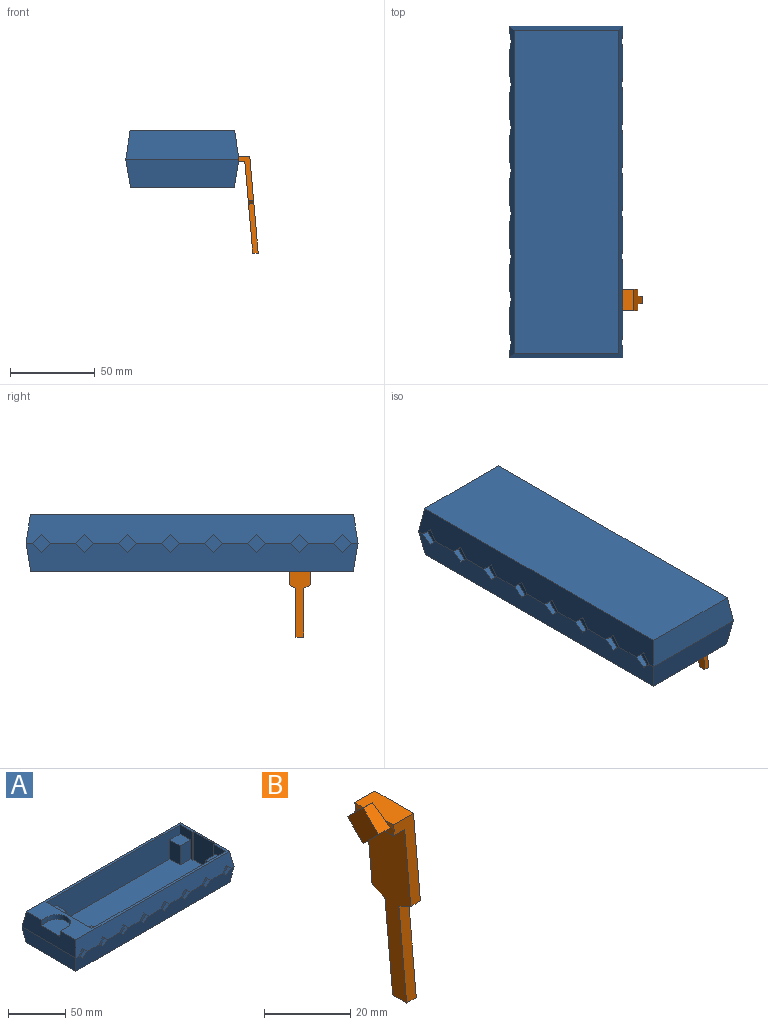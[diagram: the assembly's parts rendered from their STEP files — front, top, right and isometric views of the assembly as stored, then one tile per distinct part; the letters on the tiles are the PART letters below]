
ASSEMBLY  parts=2 mates=1
PART A: 115 faces, bbox 195.6x66.7x33.3 mm
  f0: plane 166.78x56.39mm, normal (0,0,1), area 8723mm2, adj f1,f2,f3,f12,f16,f17,f61,f62
  f1: plane 165.61x30.1mm, normal (0,1,0), area 4465.3mm2, adj f0,f3,f5,f62,f109,f111,f112,f114
  f2: plane 165.61x30.1mm, normal (0,-1,0), area 4465.3mm2, adj f0,f3,f5,f17,f103,f105,f106,f108
  f3: plane 56.39x30.1mm, normal (1,0,0), area 1177.9mm2, adj f0,f1,f2,f5,f103,f104,f112,f113
  f4: plane 190.5x61.6mm, normal (0,0,-1), area 11733.8mm2, adj f8,f9,f14,f59
  f5: plane 189.99x61.09mm, normal (0,0,1), area 1854.9mm2, adj f1,f2,f3,f6,f7,f10,f12,f13
  f6: plane 66.68x16.64mm, normal (-0.99,0,0.17), area 958.6mm2, adj f5,f8,f11,f13,f15,f58,f60
  f7: plane 66.68x16.64mm, normal (0.99,0,0.17), area 1077.7mm2, adj f5,f9,f13,f58
  f8: plane 66.68x16.64mm, normal (-0.99,0,-0.15), area 1079.4mm2, adj f4,f6,f14,f59
  f9: plane 66.68x16.64mm, normal (0.99,0,-0.15), area 1079.4mm2, adj f4,f7,f14,f59
  f10: cylinder r=11.56mm len=23.11mm, axis (0,0,1), area 184.4mm2, adj f5,f11,f15,f60
  f11: plane 23.11x19.9mm, normal (0,0,1), area 402.7mm2, adj f6,f10,f15,f60
  f12: plane 30.1x25.4mm, normal (-1,0,0), area 764.5mm2, adj f0,f5,f16,f61
  f13: plane 195.58x16.64mm, normal (0,0.99,0.17), area 3021.5mm2, adj f5,f6,f7,f14,f19,f21,f24,f26
  f14: plane 195.58x16.64mm, normal (0,0.99,-0.15), area 3018.6mm2, adj f4,f8,f9,f13,f20,f22,f25,f27
  f15: plane 8.35x5.08mm, normal (0,-1,0), area 40.2mm2, adj f5,f6,f10,f11
  f16: plane 30.1x1.17mm, normal (0,-1,0), area 35.4mm2, adj f0,f5,f12,f17
  f17: plane 30.1x15.49mm, normal (-1,0,0), area 206.7mm2, adj f0,f2,f5,f16,f106,f107
  f18: plane 10.67x10.67mm, normal (0,1,0), area 56.9mm2, adj f19,f20,f21,f22
  f19: plane 5.33x5.33mm, normal (0.71,0,-0.71), area 25.8mm2, adj f13,f18,f20,f21
  f20: plane 5.33x5.33mm, normal (0.71,0,0.71), area 26.1mm2, adj f14,f18,f19,f22
  f21: plane 5.33x5.33mm, normal (-0.71,0,-0.71), area 25.8mm2, adj f13,f18,f19,f22
  f22: plane 5.33x5.33mm, normal (-0.71,0,0.71), area 26.1mm2, adj f14,f18,f20,f21
  f23: plane 10.67x10.67mm, normal (0,1,0), area 56.9mm2, adj f24,f25,f26,f27
  f24: plane 5.33x5.33mm, normal (0.71,0,-0.71), area 25.8mm2, adj f13,f23,f25,f26
  f25: plane 5.33x5.33mm, normal (0.71,0,0.71), area 26.1mm2, adj f14,f23,f24,f27
  f26: plane 5.33x5.33mm, normal (-0.71,0,-0.71), area 25.8mm2, adj f13,f23,f24,f27
  f27: plane 5.33x5.33mm, normal (-0.71,0,0.71), area 26.1mm2, adj f14,f23,f25,f26
  f28: plane 10.67x10.67mm, normal (0,1,0), area 56.9mm2, adj f29,f30,f31,f32
  f29: plane 5.33x5.33mm, normal (0.71,0,-0.71), area 25.8mm2, adj f13,f28,f30,f31
  f30: plane 5.33x5.33mm, normal (0.71,0,0.71), area 26.1mm2, adj f14,f28,f29,f32
  f31: plane 5.33x5.33mm, normal (-0.71,0,-0.71), area 25.8mm2, adj f13,f28,f29,f32
  f32: plane 5.33x5.33mm, normal (-0.71,0,0.71), area 26.1mm2, adj f14,f28,f30,f31
  f33: plane 10.67x10.67mm, normal (0,1,0), area 56.9mm2, adj f34,f35,f36,f37
  f34: plane 5.33x5.33mm, normal (0.71,0,-0.71), area 25.8mm2, adj f13,f33,f35,f36
  f35: plane 5.33x5.33mm, normal (0.71,0,0.71), area 26.1mm2, adj f14,f33,f34,f37
  f36: plane 5.33x5.33mm, normal (-0.71,0,-0.71), area 25.8mm2, adj f13,f33,f34,f37
  f37: plane 5.33x5.33mm, normal (-0.71,0,0.71), area 26.1mm2, adj f14,f33,f35,f36
  f38: plane 10.67x10.67mm, normal (0,1,0), area 56.9mm2, adj f39,f40,f41,f42
  f39: plane 5.33x5.33mm, normal (0.71,0,-0.71), area 25.8mm2, adj f13,f38,f40,f41
  f40: plane 5.33x5.33mm, normal (0.71,0,0.71), area 26.1mm2, adj f14,f38,f39,f42
  f41: plane 5.33x5.33mm, normal (-0.71,0,-0.71), area 25.8mm2, adj f13,f38,f39,f42
  f42: plane 5.33x5.33mm, normal (-0.71,0,0.71), area 26.1mm2, adj f14,f38,f40,f41
  f43: plane 10.67x10.67mm, normal (0,1,0), area 56.9mm2, adj f44,f45,f46,f47
  f44: plane 5.33x5.33mm, normal (0.71,0,-0.71), area 25.8mm2, adj f13,f43,f45,f46
  f45: plane 5.33x5.33mm, normal (0.71,0,0.71), area 26.1mm2, adj f14,f43,f44,f47
  f46: plane 5.33x5.33mm, normal (-0.71,0,-0.71), area 25.8mm2, adj f13,f43,f44,f47
  f47: plane 5.33x5.33mm, normal (-0.71,0,0.71), area 26.1mm2, adj f14,f43,f45,f46
  f48: plane 10.67x10.67mm, normal (0,1,0), area 56.9mm2, adj f49,f50,f51,f52
  f49: plane 5.33x5.33mm, normal (0.71,0,-0.71), area 25.8mm2, adj f13,f48,f50,f51
  f50: plane 5.33x5.33mm, normal (0.71,0,0.71), area 26.1mm2, adj f14,f48,f49,f52
  f51: plane 5.33x5.33mm, normal (-0.71,0,-0.71), area 25.8mm2, adj f13,f48,f49,f52
  f52: plane 5.33x5.33mm, normal (-0.71,0,0.71), area 26.1mm2, adj f14,f48,f50,f51
  f53: plane 10.67x10.67mm, normal (0,1,0), area 56.9mm2, adj f54,f55,f56,f57
  f54: plane 5.33x5.33mm, normal (0.71,0,0.71), area 26.1mm2, adj f14,f53,f55,f56
  f55: plane 5.33x5.33mm, normal (-0.71,0,0.71), area 26.1mm2, adj f14,f53,f54,f57
  f56: plane 5.33x5.33mm, normal (0.71,0,-0.71), area 25.8mm2, adj f13,f53,f54,f57
  f57: plane 5.33x5.33mm, normal (-0.71,0,-0.71), area 25.8mm2, adj f13,f53,f55,f56
  f58: plane 195.58x16.64mm, normal (0,-0.99,0.17), area 3021.5mm2, adj f5,f6,f7,f59,f64,f66,f69,f71
  f59: plane 195.58x16.64mm, normal (0,-0.99,-0.15), area 3018.6mm2, adj f4,f8,f9,f58,f65,f67,f70,f72
  f60: plane 8.35x5.08mm, normal (0,1,0), area 40.2mm2, adj f5,f6,f10,f11
  f61: plane 30.1x1.17mm, normal (0,1,0), area 35.4mm2, adj f0,f5,f12,f62
  f62: plane 30.1x15.49mm, normal (-1,0,0), area 206.7mm2, adj f0,f1,f5,f61,f109,f110
  f63: plane 10.67x10.67mm, normal (0,-1,0), area 56.9mm2, adj f64,f65,f66,f67
  f64: plane 5.33x5.33mm, normal (0.71,0,-0.71), area 25.8mm2, adj f58,f63,f65,f66
  f65: plane 5.33x5.33mm, normal (0.71,0,0.71), area 26.1mm2, adj f59,f63,f64,f67
  f66: plane 5.33x5.33mm, normal (-0.71,0,-0.71), area 25.8mm2, adj f58,f63,f64,f67
  f67: plane 5.33x5.33mm, normal (-0.71,0,0.71), area 26.1mm2, adj f59,f63,f65,f66
  f68: plane 10.67x10.67mm, normal (0,-1,0), area 56.9mm2, adj f69,f70,f71,f72
  f69: plane 5.33x5.33mm, normal (0.71,0,-0.71), area 25.8mm2, adj f58,f68,f70,f71
  f70: plane 5.33x5.33mm, normal (0.71,0,0.71), area 26.1mm2, adj f59,f68,f69,f72
  f71: plane 5.33x5.33mm, normal (-0.71,0,-0.71), area 25.8mm2, adj f58,f68,f69,f72
  f72: plane 5.33x5.33mm, normal (-0.71,0,0.71), area 26.1mm2, adj f59,f68,f70,f71
  f73: plane 10.67x10.67mm, normal (0,-1,0), area 56.9mm2, adj f74,f75,f76,f77
  f74: plane 5.33x5.33mm, normal (0.71,0,-0.71), area 25.8mm2, adj f58,f73,f75,f76
  f75: plane 5.33x5.33mm, normal (0.71,0,0.71), area 26.1mm2, adj f59,f73,f74,f77
  f76: plane 5.33x5.33mm, normal (-0.71,0,-0.71), area 25.8mm2, adj f58,f73,f74,f77
  f77: plane 5.33x5.33mm, normal (-0.71,0,0.71), area 26.1mm2, adj f59,f73,f75,f76
  f78: plane 10.67x10.67mm, normal (0,-1,0), area 56.9mm2, adj f79,f80,f81,f82
  f79: plane 5.33x5.33mm, normal (0.71,0,-0.71), area 25.8mm2, adj f58,f78,f80,f81
  f80: plane 5.33x5.33mm, normal (0.71,0,0.71), area 26.1mm2, adj f59,f78,f79,f82
  f81: plane 5.33x5.33mm, normal (-0.71,0,-0.71), area 25.8mm2, adj f58,f78,f79,f82
  f82: plane 5.33x5.33mm, normal (-0.71,0,0.71), area 26.1mm2, adj f59,f78,f80,f81
  f83: plane 10.67x10.67mm, normal (0,-1,0), area 56.9mm2, adj f84,f85,f86,f87
  f84: plane 5.33x5.33mm, normal (0.71,0,-0.71), area 25.8mm2, adj f58,f83,f85,f86
  f85: plane 5.33x5.33mm, normal (0.71,0,0.71), area 26.1mm2, adj f59,f83,f84,f87
  f86: plane 5.33x5.33mm, normal (-0.71,0,-0.71), area 25.8mm2, adj f58,f83,f84,f87
  f87: plane 5.33x5.33mm, normal (-0.71,0,0.71), area 26.1mm2, adj f59,f83,f85,f86
  f88: plane 10.67x10.67mm, normal (0,-1,0), area 56.9mm2, adj f89,f90,f91,f92
  f89: plane 5.33x5.33mm, normal (0.71,0,-0.71), area 25.8mm2, adj f58,f88,f90,f91
  f90: plane 5.33x5.33mm, normal (0.71,0,0.71), area 26.1mm2, adj f59,f88,f89,f92
  f91: plane 5.33x5.33mm, normal (-0.71,0,-0.71), area 25.8mm2, adj f58,f88,f89,f92
  f92: plane 5.33x5.33mm, normal (-0.71,0,0.71), area 26.1mm2, adj f59,f88,f90,f91
  f93: plane 10.67x10.67mm, normal (0,-1,0), area 56.9mm2, adj f94,f95,f96,f97
  f94: plane 5.33x5.33mm, normal (0.71,0,-0.71), area 25.8mm2, adj f58,f93,f95,f96
  f95: plane 5.33x5.33mm, normal (0.71,0,0.71), area 26.1mm2, adj f59,f93,f94,f97
  f96: plane 5.33x5.33mm, normal (-0.71,0,-0.71), area 25.8mm2, adj f58,f93,f94,f97
  f97: plane 5.33x5.33mm, normal (-0.71,0,0.71), area 26.1mm2, adj f59,f93,f95,f96
  f98: plane 10.67x10.67mm, normal (0,-1,0), area 56.9mm2, adj f99,f100,f101,f102
  f99: plane 5.33x5.33mm, normal (0.71,0,0.71), area 26.1mm2, adj f59,f98,f100,f101
  f100: plane 5.33x5.33mm, normal (-0.71,0,0.71), area 26.1mm2, adj f59,f98,f99,f102
  f101: plane 5.33x5.33mm, normal (0.71,0,-0.71), area 25.8mm2, adj f58,f98,f99,f102
  f102: plane 5.33x5.33mm, normal (-0.71,0,-0.71), area 25.8mm2, adj f58,f98,f100,f101
  f103: plane 12.7x12.7mm, normal (0,0,1), area 161.3mm2, adj f2,f3,f104,f105
  f104: plane 20.45x12.7mm, normal (0,-1,0), area 259.7mm2, adj f0,f3,f103,f105
  f105: plane 20.45x12.7mm, normal (1,0,0), area 259.7mm2, adj f0,f2,f103,f104
  f106: plane 12.7x12.7mm, normal (0,0,1), area 161.3mm2, adj f2,f17,f107,f108
  f107: plane 20.45x12.7mm, normal (0,-1,0), area 259.7mm2, adj f0,f17,f106,f108
  f108: plane 20.45x12.7mm, normal (-1,0,0), area 259.7mm2, adj f0,f2,f106,f107
  f109: plane 12.7x12.7mm, normal (0,0,1), area 161.3mm2, adj f1,f62,f110,f111
  f110: plane 20.45x12.7mm, normal (0,1,0), area 259.7mm2, adj f0,f62,f109,f111
  f111: plane 20.45x12.7mm, normal (-1,0,0), area 259.7mm2, adj f0,f1,f109,f110
  f112: plane 12.7x12.7mm, normal (0,0,1), area 161.3mm2, adj f1,f3,f113,f114
  f113: plane 20.45x12.7mm, normal (0,1,0), area 259.7mm2, adj f0,f3,f112,f114
  f114: plane 20.45x12.7mm, normal (1,0,0), area 259.7mm2, adj f0,f1,f112,f113
PART B: 22 faces, bbox 15.2x12.7x60.4 mm
  f0: plane 5.08x5.08mm, normal (0,0.71,0.71), area 24.8mm2, adj f1,f2,f8,f17,f20
  f1: plane 5.08x5.08mm, normal (0,-0.71,0.71), area 24.8mm2, adj f0,f3,f8,f16,f20
  f2: plane 5.08x5.08mm, normal (0,0.71,-0.71), area 24.8mm2, adj f0,f3,f8,f19,f21
  f3: plane 5.08x5.08mm, normal (0,-0.71,-0.71), area 24.8mm2, adj f1,f2,f8,f18,f21
  f4: plane 56.93x12.7mm, normal (1,0,0.09), area 480.6mm2, adj f6,f9,f10,f11,f12,f13,f14,f15
  f5: plane 53.76x12.7mm, normal (-1,0,-0.09), area 442.4mm2, adj f6,f7,f9,f11,f12,f13,f14,f15
  f6: plane 4.57x3.19mm, normal (0,0,-1), area 14.6mm2, adj f4,f5,f13,f15
  f7: plane 12.7x3.71mm, normal (0,0,-1), area 47.1mm2, adj f5,f9,f11,f18,f19,f21
  f8: plane 10.16x10.16mm, normal (-1,0,0), area 51.6mm2, adj f0,f1,f2,f3
  f9: plane 26.21x8.89mm, normal (0,1,0), area 94mm2, adj f4,f5,f7,f10,f12,f17,f19
  f10: plane 12.7x6.62mm, normal (0,0,1), area 84mm2, adj f4,f9,f11,f16,f17,f20
  f11: plane 26.21x8.89mm, normal (0,-1,0), area 94mm2, adj f4,f5,f7,f10,f14,f16,f18
  f12: plane 4.06x3.33mm, normal (0.08,0.42,-0.9), area 14.3mm2, adj f4,f5,f9,f13
  f13: plane 29.1x5.71mm, normal (0,1,0), area 92.3mm2, adj f4,f5,f6,f12
  f14: plane 4.06x3.33mm, normal (0.08,-0.42,-0.9), area 14.3mm2, adj f4,f5,f11,f15
  f15: plane 29.1x5.71mm, normal (0,-1,0), area 92.3mm2, adj f4,f5,f6,f14
  f16: plane 2.86x1.59mm, normal (-0.99,0,-0.17), area 3.3mm2, adj f1,f10,f11,f18
  f17: plane 2.86x1.59mm, normal (-0.99,0,-0.17), area 3.3mm2, adj f0,f9,f10,f19
  f18: plane 2.86x1.59mm, normal (-0.99,0,0.17), area 3.3mm2, adj f3,f7,f11,f16
  f19: plane 2.86x1.59mm, normal (-0.99,0,0.17), area 3.3mm2, adj f2,f7,f9,f17
  f20: plane 6.99x3.49mm, normal (0.99,0,0.17), area 12.4mm2, adj f0,f1,f10
  f21: plane 6.99x3.49mm, normal (0.99,0,-0.17), area 12.4mm2, adj f2,f3,f7
PLACE A rot(axis=(-0.71,0.71,0),180deg) t=(-41.02,141.27,-12.61)mm
PLACE B t=(21.78,-20.02,-29.25)mm
MATE planar A.f68 <-> B.f8  axis (1,0,0) through (21.78,-20.02,-29.25)mm
